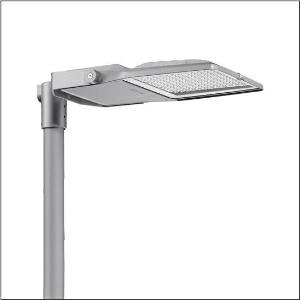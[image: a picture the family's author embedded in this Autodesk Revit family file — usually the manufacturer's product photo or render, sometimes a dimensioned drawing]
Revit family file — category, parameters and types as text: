
# Revit family: floodlight_fl_21_midi___pl52_5xa7785e2d3a_ba97
name_source: partatom
category: Lighting Fixtures
units: mm (PartAtom-declared; Revit-internal decimal feet)

## family parameters
Cut with Voids When Loaded = No
Host = Face
Light Source = No
Part Type = Normal
Room Calculation Point = No
Round Connector Dimension = Use Diameter
Shared = No

## types (1)
- --- (1 x LED, 26940 lm, 212.4 W, 3000K)
    Apparent Load = 212 VA
    CIE Flux Codes = 26 60 98 100 100
    Color Rendering = 70
    Color Temperature = 3000K
    Default Elevation = 1800 mm
    Description = Floodlight FL 21 midi, floodlight, primary light control with lens, of PMMA, primary optical cover: protective disc, of toughened safety glass, transparent, light distribution: PL52, light emission: direct distribution, installation type: surface-mounted, LED, High Power LED, rated luminous flux: 26.940lm, luminous efficacy: 127lm/W, light colour: 730, colour temperature: 3000K, control gear: ECG Smart Interface, control: flexible luminous flux parameterisation, time-dependent luminous flux control, constant luminous flux control, overheat protection, pre-setting: logarithmic dimming characteristic, with terminal, 6-pole, mains connection: 220..240V, AC, 50/60Hz, start of lifetime: 212W, end of service life: 231W, reduction: 95W, luminaire housing, of diecast aluminium, powder-coated, Siteco® metallic grey (DB 702S), sealing non-destructively replaceable, please order mast flange separately, mast bracket, of steel, galvanised, powder-coated, Siteco® metallic grey (DB 702S), Smart Interface above, protection rating (complete): IP66, insulation class (complete): insulation class II (safety insulation), certification: CE, ENEC, VDE, protection symbol: D, impact resistance: IK08, permissible operating ambient temperature: -20..+40°C, permissible operating ambient temperature for outdoor applications: -40..+50°C, standard: DIN EN 12944, LABS conformity tested according to VDMA 24364:2018-05, packaging unit: 1 piece

Light Distribution: PL52
    Height = 76 mm
    Lamp = 1 x LED
    Lamp Light Flux = 26940 lm
    Lamp Power = 212.4 W
    Lamp count = 1
    Length = 657 mm
    Luminous efficacy = 127 lm/W
    Manufacturer = Siteco
    ModVariant = No
    Model = 5XA7785E2D3A
    Number of Poles = 1
    OnlyDefault = Yes
    Power Factor = 1
    Product Name = Floodlight FL 21 midi | PL52
    Product group = floodlight | pylon annexe
    ProductGroupID = 6200
    Protection Class = Protection class II
    Protection Degree = IP 66
    RLX_Detail_Level = 1
    RLX_Emergency_Light_Flux = 0 lm
    RLX_Emergency_Type = 0
    RLX_Emergency_Type_DB = No
    RlxData = <blob elided: 153597 chars, md5=16539515>
    Socket = socket
    Standby Power = 0 W
    System Light Flux = 26940 lm
    System Power = 212 W
    Type Comments = factory setting: luminous flux: 100 % | dim-lin: 254 | 710 mA
    Type Image = l_1007123.jpg
    URL = http://relux.com
    VarID = @adj_148915
    Voltage = 0 V
    Weight = 0.00 kg
    Width = 442 mm

## geometry (parser evidence)
native form markers: Blend x4, Sweep x13
no freeform markers — native parametric forms only
